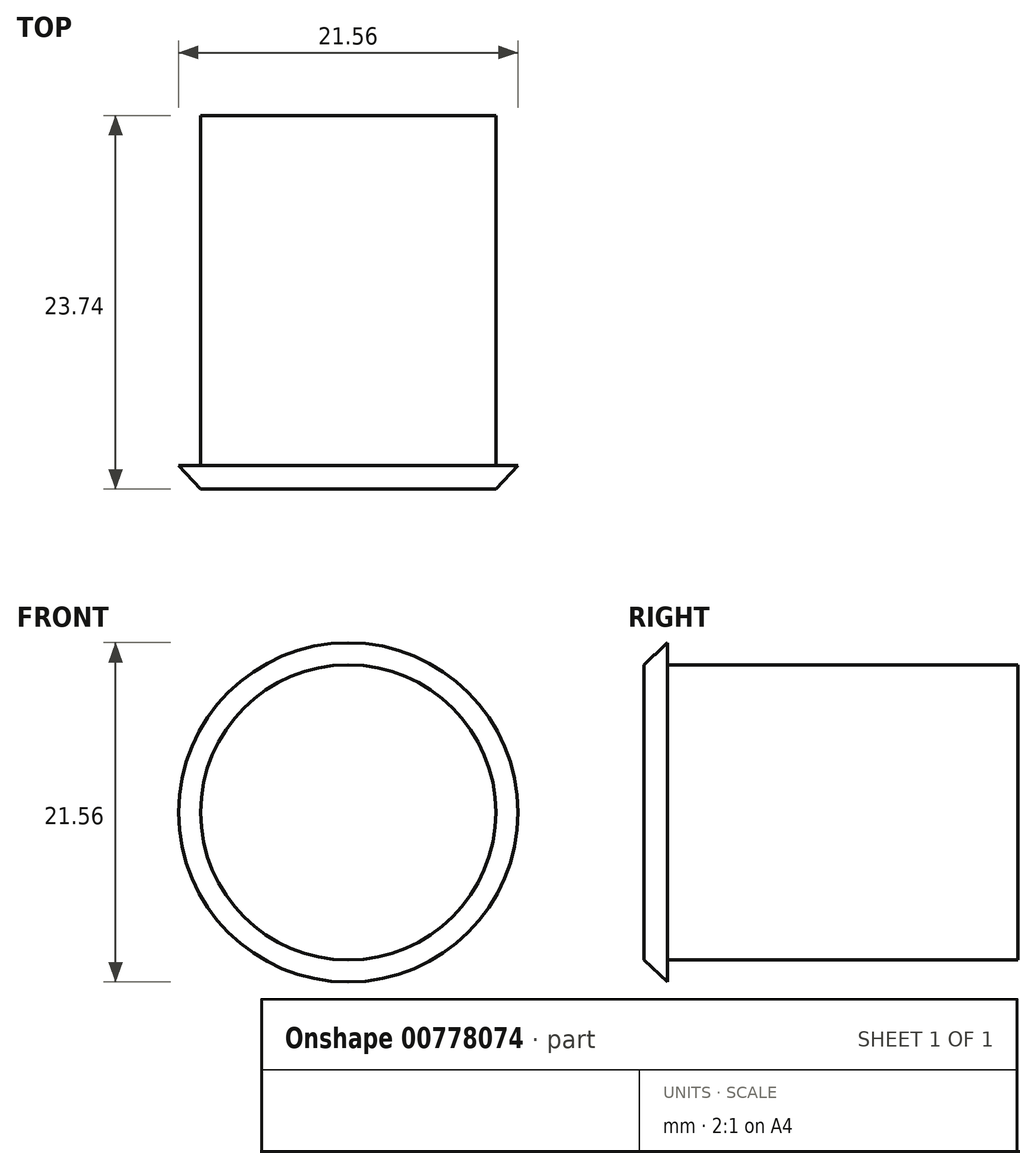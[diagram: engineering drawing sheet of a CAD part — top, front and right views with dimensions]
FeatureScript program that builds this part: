
annotation { "Feature Type Name" : "Feature", "Feature Type Description" : "" }
export const myFeature = defineFeature(function(context is Context, id is Id, definition is map)
    precondition{}
    {
        {
            var Q0;
            Q0=qCreatedBy(makeId("Right.planeOp"),FACE);
            var sketch = newSketch(context, id + "F0", { "sketchPlane" : qUnion([Q0])});
            skLineSegment(sketch, "E0", {"start": v(0, 0) * mm, "end": v(0, 9.38) * mm});
            skLineSegment(sketch, "E1", {"start": v(0, 9.38) * mm, "end": v(1.5, 10.77) * mm});
            skLineSegment(sketch, "E2", {"start": v(1.5, 10.77) * mm, "end": v(1.5, 9.37) * mm});
            skLineSegment(sketch, "E3", {"start": v(1.5, 9.38) * mm, "end": v(23.74, 9.38) * mm});
            skLineSegment(sketch, "E4", {"start": v(23.74, 9.38) * mm, "end": v(23.74, 0) * mm});
            skLineSegment(sketch, "E5", {"start": v(23.74, 0) * mm, "end": v(0, 0) * mm});
            skSolve(sketch);
        }
        {
            var Q0;
            Q0=makeQuery(id+"F0.imprint","IMPRINT",FACE,{"disambiguationData":[TD([[makeQuery(id+"F0.imprint","IMPRINT",EDGE,{"derivedFrom":sQuery(id+"F0.wireOp",EDGE,"E0")}),-1.0]])]});
            var Q1;
            Q1=sQuery(id+"F0.wireOp",EDGE,"E5");
            revolve(context, id + "F1", {"surfaceOperationType" : NewSurfaceOperationType.NEW, "entities" : qUnion([Q0]), "axis" : qUnion([Q1]), "revolveType" : RevolveType.FULL});
        }
    });
